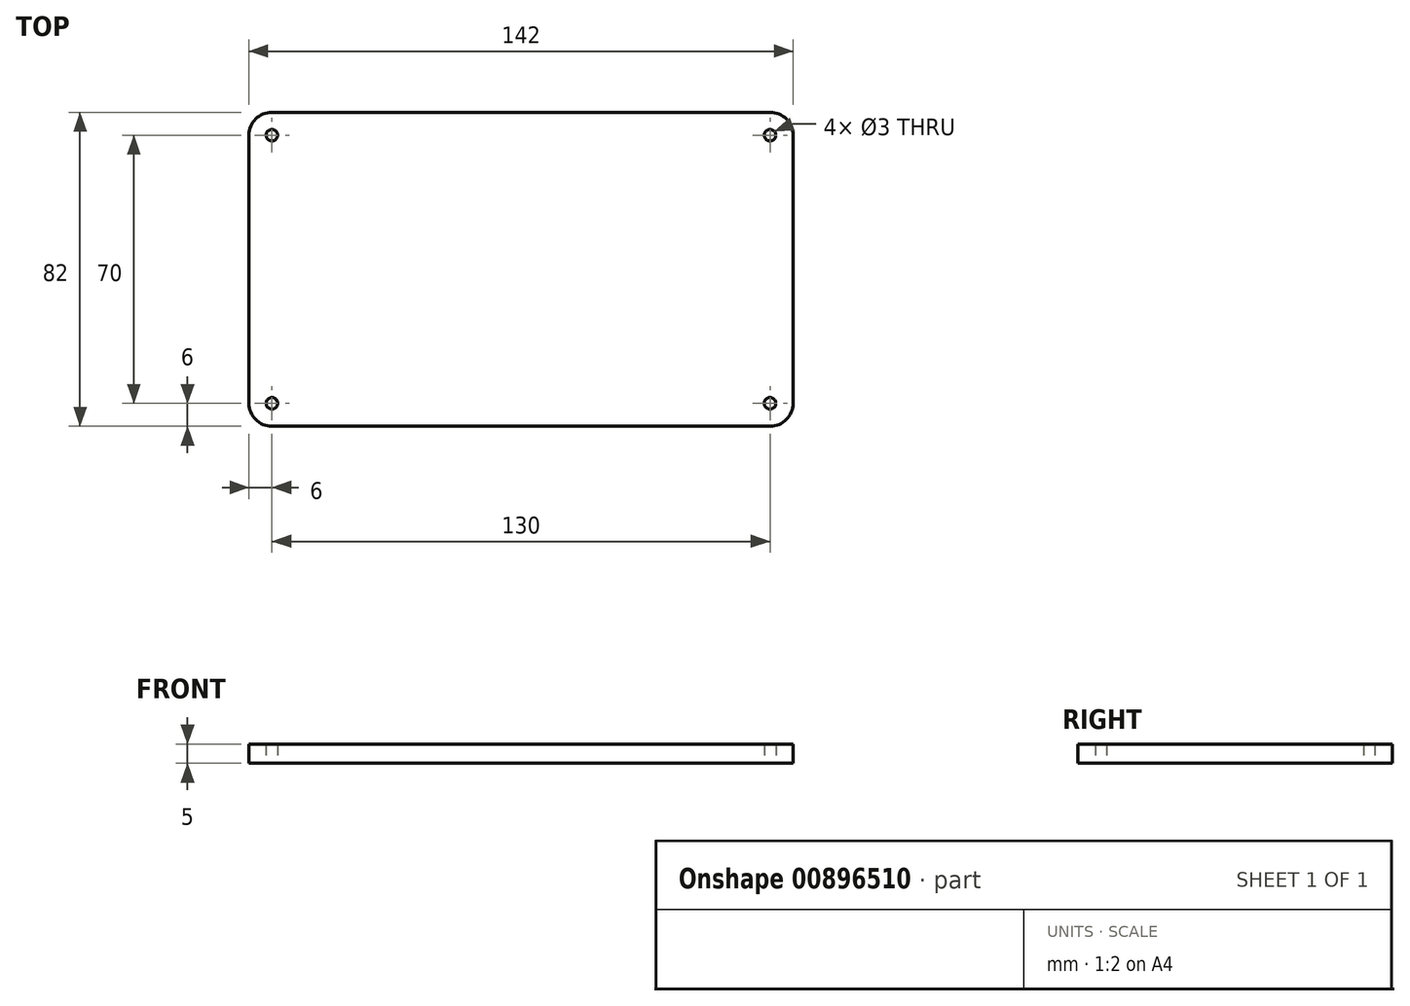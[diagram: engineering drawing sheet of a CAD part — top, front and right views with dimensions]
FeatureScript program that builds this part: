
annotation { "Feature Type Name" : "Feature", "Feature Type Description" : "" }
export const myFeature = defineFeature(function(context is Context, id is Id, definition is map)
    precondition{}
    {
        {
            var Q0;
            Q0=qCreatedBy(makeId("Top.planeOp"),FACE);
            var sketch = newSketch(context, id + "F0", { "sketchPlane" : qUnion([Q0])});
            skLineSegment(sketch, "E0.bottom", {"start": v(71, 41) * mm, "end": v(-71, 41) * mm});
            skLineSegment(sketch, "E0.top", {"start": v(71, -41) * mm, "end": v(-71, -41) * mm});
            skLineSegment(sketch, "E0.left", {"start": v(71, 41) * mm, "end": v(71, -41) * mm});
            skLineSegment(sketch, "E0.right", {"start": v(-71, 41) * mm, "end": v(-71, -41) * mm});
            skPoint(sketch, "E0.middle", {"position": v(0, 0) * mm});
            skLineSegment(sketch, "E1.bottom", {"start": v(65, 35) * mm, "end": v(-65, 35) * mm, "construction": true});
            skLineSegment(sketch, "E1.top", {"start": v(65, -35) * mm, "end": v(-65, -35) * mm, "construction": true});
            skLineSegment(sketch, "E1.left", {"start": v(65, 35) * mm, "end": v(65, -35) * mm, "construction": true});
            skLineSegment(sketch, "E1.right", {"start": v(-65, 35) * mm, "end": v(-65, -35) * mm, "construction": true});
            skCircle(sketch, "E2", {"center": v(-65, 35) * mm, "radius": 1.5 * mm});
            skCircle(sketch, "E3", {"center": v(65, 35) * mm, "radius": 1.5 * mm});
            skCircle(sketch, "E4", {"center": v(65, -35) * mm, "radius": 1.5 * mm});
            skCircle(sketch, "E5", {"center": v(-65, -35) * mm, "radius": 1.5 * mm});
            skSolve(sketch);
        }
        {
            var Q0;
            Q0 = qSketchRegion(id + "F0", true);
            extrude(context, id + "F1", {"entities" : qUnion([Q0]), "depth" : 5 * mm, "offsetDistance" : 25 * mm});
        }
        {
            var Q0;
            Q0=makeQuery(id+"F1.opExtrude","SWEPT_EDGE",EDGE,{"disambiguationData":[OSD([sQuery(id+"F0.wireOp",EDGE,"E0.top"),sQuery(id+"F0.wireOp",EDGE,"E0.right")])]});
            var Q1;
            Q1=makeQuery(id+"F1.opExtrude","SWEPT_EDGE",EDGE,{"disambiguationData":[OSD([sQuery(id+"F0.wireOp",EDGE,"E0.bottom"),sQuery(id+"F0.wireOp",EDGE,"E0.right")])]});
            var Q2;
            Q2=makeQuery(id+"F1.opExtrude","SWEPT_EDGE",EDGE,{"disambiguationData":[OSD([sQuery(id+"F0.wireOp",EDGE,"E0.bottom"),sQuery(id+"F0.wireOp",EDGE,"E0.left")])]});
            var Q3;
            Q3=makeQuery(id+"F1.opExtrude","SWEPT_EDGE",EDGE,{"disambiguationData":[OSD([sQuery(id+"F0.wireOp",EDGE,"E0.top"),sQuery(id+"F0.wireOp",EDGE,"E0.left")])]});
            fillet(context, id + "F2", {"entities" : qUnion([Q0, Q1, Q2, Q3]), "radius" : 6 * mm, "tangentPropagation" : true, "allowEdgeOverflow" : false});
        }
    });
